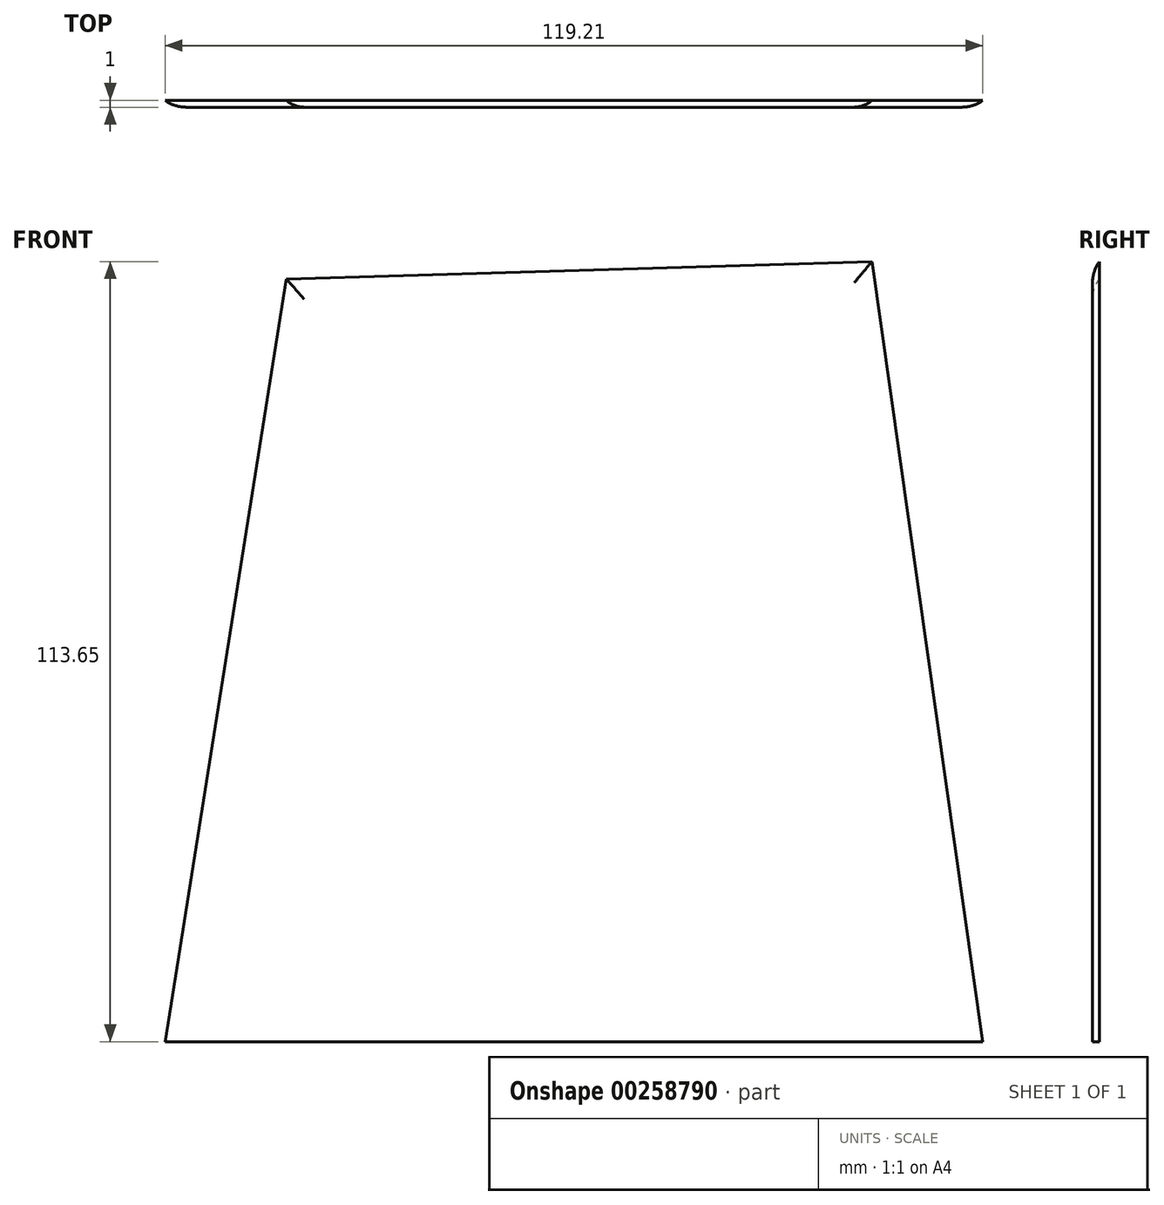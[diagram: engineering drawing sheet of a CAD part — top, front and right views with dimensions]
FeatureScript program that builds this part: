
annotation { "Feature Type Name" : "Feature", "Feature Type Description" : "" }
export const myFeature = defineFeature(function(context is Context, id is Id, definition is map)
    precondition{}
    {
        {
            var Q0;
            Q0=qCreatedBy(makeId("Front.planeOp"),FACE);
            var sketch = newSketch(context, id + "F0", { "sketchPlane" : qUnion([Q0])});
            skLineSegment(sketch, "E0", {"start": v(-41.42, 62.38) * mm, "end": v(-59.1, -48.74) * mm});
            skLineSegment(sketch, "E1", {"start": v(-59.1, -48.74) * mm, "end": v(60.1, -48.74) * mm});
            skLineSegment(sketch, "E2", {"start": v(60.1, -48.74) * mm, "end": v(43.95, 64.9) * mm});
            skLineSegment(sketch, "E3", {"start": v(43.95, 64.9) * mm, "end": v(-41.42, 62.38) * mm});
            skSolve(sketch);
        }
        {
            var Q0;
            Q0=makeQuery(id+"F0.imprint","IMPRINT",FACE,{"disambiguationData":[TD([[makeQuery(id+"F0.imprint","IMPRINT",EDGE,{"derivedFrom":sQuery(id+"F0.wireOp",EDGE,"E0")}),1.0]])]});
            extrude(context, id + "F1", {"entities" : qUnion([Q0]), "depth" : 1 * mm});
        }
        {
            var Q0;
            Q0=makeQuery(id+"F1.opExtrude","CAP_EDGE",EDGE,{"disambiguationData":[OSD([sQuery(id+"F0.wireOp",EDGE,"E0")])],"isStart":false});
            var Q1;
            Q1=makeQuery(id+"F1.opExtrude","CAP_EDGE",EDGE,{"disambiguationData":[OSD([sQuery(id+"F0.wireOp",EDGE,"E2")])],"isStart":false});
            var Q2;
            Q2=makeQuery(id+"F1.opExtrude","CAP_EDGE",EDGE,{"disambiguationData":[OSD([sQuery(id+"F0.wireOp",EDGE,"E3")])],"isStart":false});
            fillet(context, id + "F2", {"entities" : qUnion([Q0, Q1, Q2]), "radius" : 5 * mm, "tangentPropagation" : true, "allowEdgeOverflow" : false});
        }
    });
